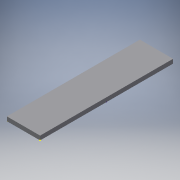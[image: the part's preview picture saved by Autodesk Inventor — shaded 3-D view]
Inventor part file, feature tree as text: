
AUTODESK INVENTOR PART (.ipt)
format: ipt  version: 2017 (Build 210142000, 142)  size: 104,960 bytes
history: native  units: in
note: dims shown in document units (in); Inventor stores cm internally (conversion verified against a paired STEP export)
features: sketch x4, extrude x2, reference x2, other x2
ambient origin geometry x8: Origin, YZ Plane, XZ Plane, XY Plane, X Axis, Y Axis, Z Axis, Center Point
bodies: Solid1 (feature_tree)
feature tree (10):
  extrude  "Extrusion1"  Depth=1.0in
  sketch  "Sketch2"  dims[d4=0.125in d5=0.0in d6=0.9375in d7=0.0in]
  sketch  "Sketch3"
  extrude  "Extrusion2"  Depth=0.125in TaperAngle=0.0deg
  sketch  "Sketch1"  dims[d0=4.0in d1=1.0in]
  sketch  "Sketch4"
  reference  "Reference1"
  reference  "Reference2"
  other  "Robot Frame '16.iam"
  other  "tetrix_739089_2012:2"
